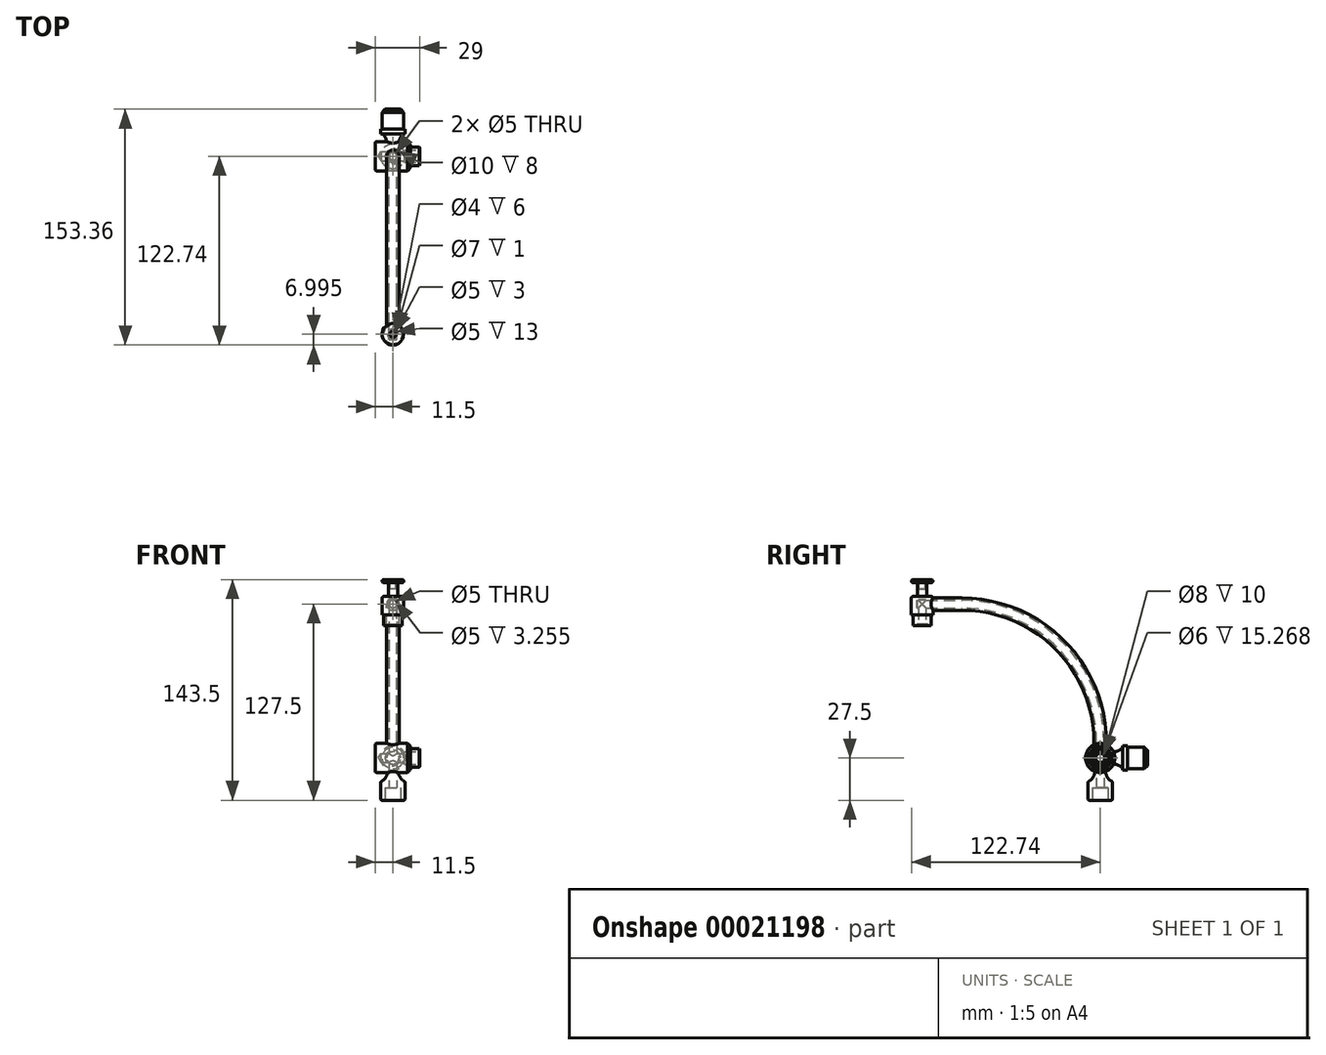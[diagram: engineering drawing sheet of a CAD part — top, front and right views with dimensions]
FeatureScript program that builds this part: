
annotation { "Feature Type Name" : "Feature", "Feature Type Description" : "" }
export const myFeature = defineFeature(function(context is Context, id is Id, definition is map)
    precondition{}
    {
        {
            var Q0;
            Q0=qCreatedBy(makeId("Right.planeOp"),FACE);
            var sketch = newSketch(context, id + "F0", { "sketchPlane" : qUnion([Q0])});
            skCircle(sketch, "E0", {"center": v(0, 0) * mm, "radius": 9.5 * mm});
            skSolve(sketch);
        }
        {
            var Q0;
            Q0=qSketchRegion(id+"F0",true);
            extrude(context, id + "F1", {"entities" : qUnion([Q0]), "endBound" : BoundingType.SYMMETRIC, "depth" : 23 * mm});
        }
        {
            var Q0;
            Q0=makeQuery(id+"F1.opExtrude","CAP_EDGE",EDGE,{"disambiguationData":[OSD([sQuery(id+"F0.wireOp",EDGE,"E0")])],"isStart":false});
            chamfer(context, id + "F2", {"entities" : qUnion([Q0]), "width" : 2 * mm, "tangentPropagation" : true});
        }
        {
            var Q0;
            Q0=makeQuery(id+"F1.opExtrude","CAP_FACE",FACE,{"disambiguationData":[OSD([sQuery(id+"F0.wireOp",EDGE,"E0")])],"isStart":false});
            var sketch = newSketch(context, id + "F3", { "sketchPlane" : qUnion([Q0])});
            skCircle(sketch, "E1", {"center": v(0, 0) * mm, "radius": 6 * mm});
            skSolve(sketch);
        }
        {
            var Q0;
            Q0=makeQuery(id+"F3.imprint","IMPRINT",FACE,{"disambiguationData":[TD([[makeQuery(id+"F3.imprint","IMPRINT",EDGE,{"derivedFrom":sQuery(id+"F3.wireOp",EDGE,"E1")}),1.0]])]});
            extrude(context, id + "F4", {"entities" : qUnion([Q0]), "operationType" : NewBodyOperationType.ADD, "depth" : 6 * mm});
        }
        {
            var Q0;
            Q0=makeQuery(id+"F1.opExtrude","CAP_EDGE",EDGE,{"disambiguationData":[OSD([sQuery(id+"F0.wireOp",EDGE,"E0")])],"isStart":true});
            fillet(context, id + "F5", {"entities" : qUnion([Q0]), "radius" : 1 * mm, "tangentPropagation" : true, "allowEdgeOverflow" : false});
        }
        {
            var Q0;
            Q0=qCreatedBy(makeId("Front.planeOp"),FACE);
            var sketch = newSketch(context, id + "F6", { "sketchPlane" : qUnion([Q0])});
            skLineSegment(sketch, "E2", {"start": v(-17.5, 0) * mm, "end": v(17.5, 0) * mm, "construction": true});
            skLineSegment(sketch, "E3", {"start": v(-9.5, 0) * mm, "end": v(-7.77, 3) * mm});
            skLineSegment(sketch, "E4", {"start": v(-7.77, 3) * mm, "end": v(7.5, 3) * mm});
            skLineSegment(sketch, "E5", {"start": v(7.5, 3) * mm, "end": v(7.5, 4) * mm});
            skLineSegment(sketch, "E6", {"start": v(7.5, 4) * mm, "end": v(17.5, 4) * mm});
            skLineSegment(sketch, "E7", {"start": v(17.5, 4) * mm, "end": v(17.5, 0) * mm});
            skLineSegment(sketch, "E8.0.MirrorCS", {"start": v(17.5, -4) * mm, "end": v(17.5, 0) * mm, "construction": true});
            skLineSegment(sketch, "E8.1.MirrorCS", {"start": v(7.5, -3) * mm, "end": v(7.5, -4) * mm, "construction": true});
            skLineSegment(sketch, "E8.2.MirrorCS", {"start": v(7.5, -4) * mm, "end": v(17.5, -4) * mm, "construction": true});
            skLineSegment(sketch, "E8.3.MirrorCS", {"start": v(-7.77, -3) * mm, "end": v(7.5, -3) * mm, "construction": true});
            skLineSegment(sketch, "E8.4.MirrorCS", {"start": v(-9.5, 0) * mm, "end": v(-7.77, -3) * mm, "construction": true});
            skLineSegment(sketch, "E9", {"start": v(-9.5, 0) * mm, "end": v(17.5, 0) * mm});
            skSolve(sketch);
        }
        {
            var Q0;
            Q0=qSketchRegion(id+"F6",true);
            var Q1;
            Q1=sQuery(id+"F6.wireOp",EDGE,"E2");
            revolve(context, id + "F7", {"operationType" : NewBodyOperationType.REMOVE, "entities" : qUnion([Q0]), "axis" : qUnion([Q1]), "revolveType" : RevolveType.FULL, "oppositeDirection" : true});
        }
        {
            var Q0;
            Q0=qCreatedBy(makeId("Front.planeOp"),FACE);
            var sketch = newSketch(context, id + "F8", { "sketchPlane" : qUnion([Q0])});
            skLineSegment(sketch, "E10", {"start": v(0, 0) * mm, "end": v(0, -27.5) * mm, "construction": true});
            skLineSegment(sketch, "E11", {"start": v(0, -27.5) * mm, "end": v(8, -27.5) * mm});
            skLineSegment(sketch, "E12", {"start": v(8, -27.5) * mm, "end": v(8, -15.5) * mm});
            skArc(sketch, "E13", {"start": v(3.5, -8.5) * mm, "mid": v(4.72, -12.66) * mm, "end": v(8, -15.5) * mm});
            skLineSegment(sketch, "E14", {"start": v(3.5, -8.5) * mm, "end": v(0, -8.5) * mm});
            skLineSegment(sketch, "E15", {"start": v(3.5, -8.5) * mm, "end": v(3.5, -3) * mm, "construction": true});
            skLineSegment(sketch, "E16", {"start": v(0, -8.5) * mm, "end": v(0, -27.5) * mm});
            skSolve(sketch);
        }
        {
            var Q0;
            Q0=makeQuery(id+"F8.imprint","IMPRINT",FACE,{"disambiguationData":[TD([[makeQuery(id+"F8.imprint","IMPRINT",EDGE,{"derivedFrom":sQuery(id+"F8.wireOp",EDGE,"E11")}),1.0]])]});
            var Q1;
            Q1=sQuery(id+"F8.wireOp",EDGE,"E10");
            revolve(context, id + "F9", {"operationType" : NewBodyOperationType.ADD, "entities" : qUnion([Q0]), "axis" : qUnion([Q1]), "revolveType" : RevolveType.FULL});
        }
        {
            var Q0;
            Q0=makeQuery(id+"F9.opRevolve","SWEPT_FACE",FACE,{"disambiguationData":[OSD([sQuery(id+"F8.wireOp",EDGE,"E11")])]});
            var sketch = newSketch(context, id + "F10", { "sketchPlane" : qUnion([Q0])});
            skCircle(sketch, "E17", {"center": v(0, 0) * mm, "radius": 2.5 * mm});
            skSolve(sketch);
        }
        {
            var Q0;
            Q0=qSketchRegion(id+"F10",true);
            extrude(context, id + "F11", {"entities" : qUnion([Q0]), "operationType" : NewBodyOperationType.REMOVE, "endBound" : BoundingType.THROUGH_ALL, "oppositeDirection" : true, "depth" : 25 * mm});
        }
        {
            var Q0;
            Q0=makeQuery(id+"F9.opRevolve","SWEPT_FACE",FACE,{"disambiguationData":[OSD([sQuery(id+"F8.wireOp",EDGE,"E11")])]});
            var sketch = newSketch(context, id + "F12", { "sketchPlane" : qUnion([Q0])});
            skCircle(sketch, "E18", {"center": v(0, 0) * mm, "radius": 5 * mm});
            skSolve(sketch);
        }
        {
            var Q0;
            Q0=qSketchRegion(id+"F12",true);
            extrude(context, id + "F13", {"entities" : qUnion([Q0]), "operationType" : NewBodyOperationType.REMOVE, "oppositeDirection" : true, "depth" : 8 * mm});
        }
        {
            var Q0;
            Q0=qCreatedBy(makeId("Right.planeOp"),FACE);
            var sketch = newSketch(context, id + "F14", { "sketchPlane" : qUnion([Q0])});
            skLineSegment(sketch, "E19", {"start": v(0, 0) * mm, "end": v(31.4, 0) * mm, "construction": true});
            skLineSegment(sketch, "E20", {"start": v(17.62, 8) * mm, "end": v(14.62, 8) * mm});
            skLineSegment(sketch, "E21", {"start": v(14.62, 8) * mm, "end": v(14.62, 7) * mm});
            skArc(sketch, "E22", {"start": v(8.62, 4) * mm, "mid": v(11.97, 4.8) * mm, "end": v(14.62, 7) * mm});
            skLineSegment(sketch, "E23", {"start": v(8.62, 4) * mm, "end": v(8.62, 0) * mm});
            skLineSegment(sketch, "E24", {"start": v(8.62, 4) * mm, "end": v(4.18, 4) * mm, "construction": true});
            skLineSegment(sketch, "E25", {"start": v(17.62, 8) * mm, "end": v(17.62, 7) * mm});
            skLineSegment(sketch, "E26", {"start": v(17.62, 7) * mm, "end": v(30.62, 7) * mm});
            skLineSegment(sketch, "E27", {"start": v(30.62, 7) * mm, "end": v(30.62, 0) * mm});
            skLineSegment(sketch, "E28", {"start": v(30.62, 0) * mm, "end": v(8.62, 0) * mm});
            skSolve(sketch);
        }
        {
            var Q0;
            Q0=qSketchRegion(id+"F14",true);
            var Q1;
            Q1=sQuery(id+"F14.wireOp",EDGE,"E19");
            revolve(context, id + "F15", {"operationType" : NewBodyOperationType.ADD, "entities" : qUnion([Q0]), "axis" : qUnion([Q1]), "revolveType" : RevolveType.FULL});
        }
        {
            var Q0;
            Q0=makeQuery(id+"F15.opRevolve","SWEPT_EDGE",EDGE,{"disambiguationData":[OSD([sQuery(id+"F14.wireOp",EDGE,"E26"),sQuery(id+"F14.wireOp",EDGE,"E27")])]});
            chamfer(context, id + "F16", {"entities" : qUnion([Q0]), "width" : 2 * mm, "tangentPropagation" : true});
        }
        {
            var Q0;
            Q0=makeQuery(id+"F9.opRevolve","SWEPT_EDGE",EDGE,{"disambiguationData":[OSD([sQuery(id+"F8.wireOp",EDGE,"E12"),sQuery(id+"F8.wireOp",EDGE,"E13")])]});
            var Q1;
            Q1=makeQuery(id+"F9.opRevolve","SWEPT_EDGE",EDGE,{"disambiguationData":[OSD([sQuery(id+"F8.wireOp",EDGE,"E11"),sQuery(id+"F8.wireOp",EDGE,"E12")])]});
            fillet(context, id + "F17", {"entities" : qUnion([Q0, Q1]), "radius" : 1 * mm, "tangentPropagation" : true, "allowEdgeOverflow" : false});
        }
        {
            var Q0;
            Q0=qCreatedBy(makeId("Right.planeOp"),FACE);
            var sketch = newSketch(context, id + "F18", { "sketchPlane" : qUnion([Q0])});
            skLineSegment(sketch, "E29", {"start": v(0, 0) * mm, "end": v(0, 8) * mm, "construction": true});
            skLineSegment(sketch, "E30", {"start": v(0, 8) * mm, "end": v(0, 10) * mm});
            skArc(sketch, "E31", {"start": v(0, 10) * mm, "mid": v(-26.36, 73.64) * mm, "end": v(-90, 100) * mm});
            skLineSegment(sketch, "E32", {"start": v(-90, 100) * mm, "end": v(-110, 100) * mm});
            skSolve(sketch);
        }
        {
            var Q0;
            Q0=qCreatedBy(makeId("Front.planeOp"),FACE);
            var Q1;
            Q1=sQuery(id+"F18.wireOp",VERTEX,"E32.end");
            cPlane(context, id + "F19", {"entities" : qUnion([Q0, Q1]), "cplaneType" : CPlaneType.PLANE_POINT, "offset" : 150 * mm, "width" : 150 * mm, "height" : 150 * mm});
        }
        {
            var Q0;
            Q0=qCreatedBy(id+"F19.planeOp",FACE);
            var sketch = newSketch(context, id + "F20", { "sketchPlane" : qUnion([Q0])});
            skPoint(sketch, "E33.0", {"position": v(0, 100) * mm});
            skCircle(sketch, "E34", {"center": v(0, 100) * mm, "radius": 4 * mm});
            skCircle(sketch, "E35", {"center": v(0, 100) * mm, "radius": 2.5 * mm});
            skSolve(sketch);
        }
        {
            var Q0;
            Q0=makeQuery(id+"F20.imprint","IMPRINT",FACE,{"disambiguationData":[TD([[makeQuery(id+"F20.imprint","IMPRINT",EDGE,{"derivedFrom":sQuery(id+"F20.wireOp",EDGE,"E34")}),1.0]])]});
            var Q1;
            Q1=sQuery(id+"F18.wireOp",EDGE,"E32");
            var Q2;
            Q2=sQuery(id+"F18.wireOp",EDGE,"E31");
            var Q3;
            Q3=sQuery(id+"F18.wireOp",EDGE,"E30");
            sweep(context, id + "F21", {"operationType" : NewBodyOperationType.ADD, "profiles" : qUnion([Q0]), "path" : qUnion([Q1, Q2, Q3])});
        }
        {
            var Q0;
            Q0=qCreatedBy(makeId("Top.planeOp"),FACE);
            var Q1;
            Q1=sQuery(id+"F18.wireOp",VERTEX,"E32.end");
            cPlane(context, id + "F22", {"entities" : qUnion([Q0, Q1]), "cplaneType" : CPlaneType.PLANE_POINT, "offset" : 150 * mm, "width" : 150 * mm, "height" : 150 * mm});
        }
        {
            var Q0;
            Q0=qCreatedBy(id+"F22.planeOp",FACE);
            var sketch = newSketch(context, id + "F23", { "sketchPlane" : qUnion([Q0])});
            skCircle(sketch, "E36", {"center": v(0, -115.74) * mm, "radius": 7 * mm});
            skLineSegment(sketch, "E37.0", {"start": v(4, -110) * mm, "end": v(-4, -110) * mm, "construction": true});
            skSolve(sketch);
        }
        {
            var Q0;
            Q0=qSketchRegion(id+"F23",true);
            extrude(context, id + "F24", {"entities" : qUnion([Q0]), "operationType" : NewBodyOperationType.ADD, "depth" : 5 * mm, "hasSecondDirection" : true, "secondDirectionOppositeDirection" : true, "secondDirectionDepth" : 7 * mm});
        }
        {
            var Q0;
            Q0=makeQuery(id+"F20.imprint","IMPRINT",FACE,{"disambiguationData":[TD([[makeQuery(id+"F20.imprint","IMPRINT",EDGE,{"derivedFrom":sQuery(id+"F20.wireOp",EDGE,"E35")}),1.0]])]});
            extrude(context, id + "F25", {"entities" : qUnion([Q0]), "operationType" : NewBodyOperationType.REMOVE, "endBound" : BoundingType.UP_TO_NEXT, "oppositeDirection" : true, "depth" : 5 * mm, "hasSecondDirection" : true, "secondDirectionOppositeDirection" : false, "secondDirectionDepth" : 9 * mm});
        }
        {
            var Q0;
            Q0=makeQuery(id+"F24.opExtrude","CAP_FACE",FACE,{"disambiguationData":[OSD([sQuery(id+"F23.wireOp",EDGE,"E36")])],"isStart":false});
            var sketch = newSketch(context, id + "F26", { "sketchPlane" : qUnion([Q0])});
            skCircle(sketch, "E38", {"center": v(0, -115.74) * mm, "radius": 3 * mm});
            skSolve(sketch);
        }
        {
            var Q0;
            Q0=qSketchRegion(id+"F26",true);
            extrude(context, id + "F27", {"entities" : qUnion([Q0]), "operationType" : NewBodyOperationType.ADD, "depth" : 9 * mm});
        }
        {
            var Q0;
            Q0=makeQuery(id+"F27.opExtrude","CAP_FACE",FACE,{"disambiguationData":[OSD([sQuery(id+"F26.wireOp",EDGE,"E38")])],"isStart":false});
            var sketch = newSketch(context, id + "F28", { "sketchPlane" : qUnion([Q0])});
            skCircle(sketch, "E39", {"center": v(0, -115.74) * mm, "radius": 7 * mm});
            skSolve(sketch);
        }
        {
            var Q0;
            Q0=qSketchRegion(id+"F28",true);
            extrude(context, id + "F29", {"entities" : qUnion([Q0]), "operationType" : NewBodyOperationType.ADD, "depth" : 2 * mm});
        }
        {
            var Q0;
            Q0=makeQuery(id+"F29.opExtrude","CAP_EDGE",EDGE,{"disambiguationData":[OSD([sQuery(id+"F28.wireOp",EDGE,"E39")])],"isStart":false});
            var Q1;
            Q1=makeQuery(id+"F29.opExtrude","CAP_EDGE",EDGE,{"disambiguationData":[OSD([sQuery(id+"F28.wireOp",EDGE,"E39")])],"isStart":true});
            var Q2;
            Q2=makeQuery(id+"F27.opExtrude","CAP_EDGE",EDGE,{"disambiguationData":[OSD([sQuery(id+"F26.wireOp",EDGE,"E38")])],"isStart":false});
            var Q3;
            Q3=makeQuery(id+"F27.opExtrude","CAP_EDGE",EDGE,{"disambiguationData":[OSD([sQuery(id+"F26.wireOp",EDGE,"E38")])],"isStart":true});
            var Q4;
            Q4=makeQuery(id+"F24.opExtrude","CAP_EDGE",EDGE,{"disambiguationData":[OSD([sQuery(id+"F23.wireOp",EDGE,"E36")])],"isStart":false});
            fillet(context, id + "F30", {"entities" : qUnion([Q0, Q1, Q2, Q3, Q4]), "radius" : 1 * mm, "tangentPropagation" : true, "allowEdgeOverflow" : false});
        }
        {
            var Q0;
            Q0=makeQuery(id+"F29.opExtrude","CAP_FACE",FACE,{"disambiguationData":[OSD([sQuery(id+"F28.wireOp",EDGE,"E39")])],"isStart":false});
            var sketch = newSketch(context, id + "F31", { "sketchPlane" : qUnion([Q0])});
            skCircle(sketch, "E40", {"center": v(0, -115.74) * mm, "radius": 2 * mm});
            skSolve(sketch);
        }
        {
            var Q0;
            Q0=makeQuery(id+"F31.imprint","IMPRINT",FACE,{"disambiguationData":[TD([[makeQuery(id+"F31.imprint","IMPRINT",EDGE,{"derivedFrom":sQuery(id+"F31.wireOp",EDGE,"E40")}),1.0]])]});
            extrude(context, id + "F32", {"entities" : qUnion([Q0]), "operationType" : NewBodyOperationType.REMOVE, "oppositeDirection" : true, "depth" : 6 * mm});
        }
        {
            var Q0;
            Q0=makeQuery(id+"F24.opExtrude","CAP_FACE",FACE,{"disambiguationData":[OSD([sQuery(id+"F23.wireOp",EDGE,"E36")])],"isStart":true});
            var sketch = newSketch(context, id + "F33", { "sketchPlane" : qUnion([Q0])});
            skCircle(sketch, "E41", {"center": v(0, 115.74) * mm, "radius": 6 * mm});
            skSolve(sketch);
        }
        {
            var Q0;
            Q0=qSketchRegion(id+"F33",true);
            extrude(context, id + "F34", {"entities" : qUnion([Q0]), "operationType" : NewBodyOperationType.ADD, "depth" : 7 * mm});
        }
        {
            var Q0;
            Q0=makeQuery(id+"F34.opExtrude","CAP_FACE",FACE,{"disambiguationData":[OSD([sQuery(id+"F33.wireOp",EDGE,"E41")])],"isStart":false});
            var sketch = newSketch(context, id + "F35", { "sketchPlane" : qUnion([Q0])});
            skCircle(sketch, "E42", {"center": v(0, 115.74) * mm, "radius": 3.5 * mm});
            skSolve(sketch);
        }
        {
            var Q0;
            Q0=makeQuery(id+"F35.imprint","IMPRINT",FACE,{"disambiguationData":[TD([[makeQuery(id+"F35.imprint","IMPRINT",EDGE,{"derivedFrom":sQuery(id+"F35.wireOp",EDGE,"E42")}),1.0]])]});
            extrude(context, id + "F36", {"entities" : qUnion([Q0]), "operationType" : NewBodyOperationType.REMOVE, "oppositeDirection" : true, "depth" : 1 * mm});
        }
        {
            var Q0;
            Q0=makeQuery(id+"F36.boolean.opBoolean","COPY",FACE,{"derivedFrom":makeQuery(id+"F36.opExtrude","CAP_FACE",FACE,{"disambiguationData":[OSD([sQuery(id+"F35.wireOp",EDGE,"E42")])],"isStart":false})});
            var sketch = newSketch(context, id + "F37", { "sketchPlane" : qUnion([Q0])});
            skCircle(sketch, "E43", {"center": v(0, 115.74) * mm, "radius": 2.5 * mm});
            skSolve(sketch);
        }
        {
            var Q0;
            Q0=makeQuery(id+"F37.imprint","IMPRINT",FACE,{"disambiguationData":[TD([[makeQuery(id+"F37.imprint","IMPRINT",EDGE,{"derivedFrom":sQuery(id+"F37.wireOp",EDGE,"E43")}),1.0]])]});
            extrude(context, id + "F38", {"entities" : qUnion([Q0]), "operationType" : NewBodyOperationType.REMOVE, "oppositeDirection" : true, "depth" : 16 * mm});
        }
        {
            var Q0;
            Q0=makeQuery(id+"F4.opExtrude","CAP_EDGE",EDGE,{"disambiguationData":[OSD([sQuery(id+"F3.wireOp",EDGE,"E1")])],"isStart":false});
            chamfer(context, id + "F39", {"entities" : qUnion([Q0]), "width" : 0.5 * mm, "tangentPropagation" : true});
        }
    });
